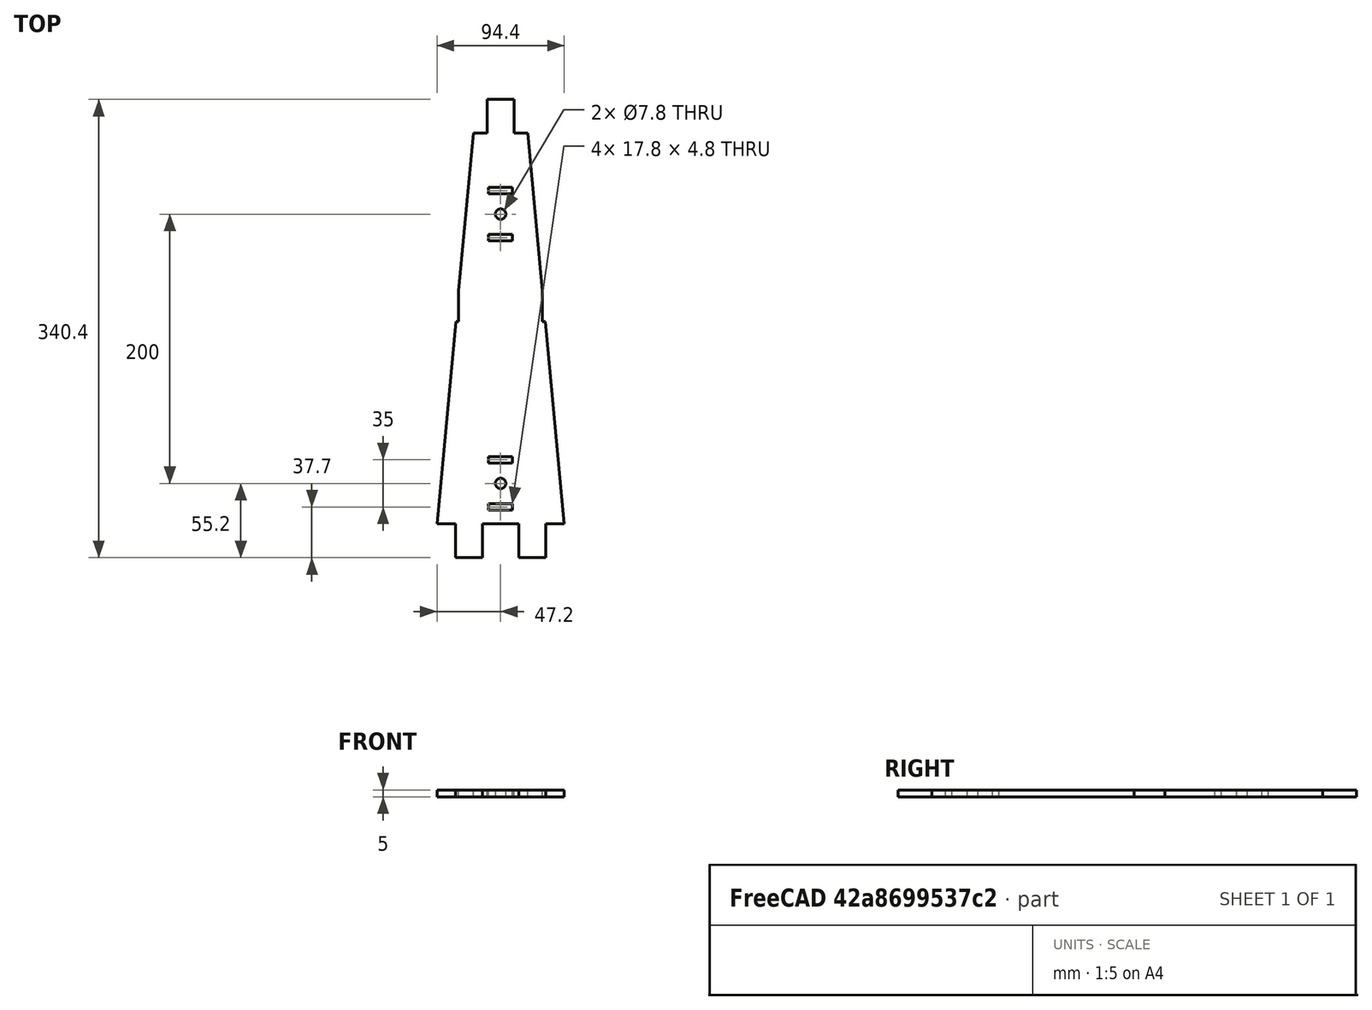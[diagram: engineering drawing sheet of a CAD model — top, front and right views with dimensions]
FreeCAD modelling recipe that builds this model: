
FCSTD DOCUMENT  (FreeCAD 0.16R6712 (Git))
Label: VerticalModded
License: All rights reserved
LicenseURL: http://en.wikipedia.org/wiki/All_rights_reserved
objects: Sketcher::SketchObject×1, PartDesign::Pad×1
note: 3 computed .brp shape members not serialized (recipe doc carries the construction recipe); baked Part::Feature solids carry a one-line shape summary decoded from their .brp

FEATURE [Sketcher::SketchObject] Sketch010
  sketch-geometry (45):
    g0: LineSegment StartX=-10.1 StartY=160.1 StartZ=0 EndX=-20.2 EndY=160.1 EndZ=0
    g1: LineSegment StartX=-20.2 StartY=160.1 StartZ=0 EndX=-31.1 EndY=42.9452 EndZ=0
    g2: LineSegment StartX=-47.2 StartY=-130.1 StartZ=0 EndX=-33.6 EndY=-130.1 EndZ=0
    g3: LineSegment StartX=-33.6 StartY=-130.1 StartZ=0 EndX=-33.6 EndY=-155.2 EndZ=0
    g4: LineSegment StartX=-33.6 StartY=-155.2 StartZ=0 EndX=-13.4 EndY=-155.2 EndZ=0
    g5: LineSegment StartX=-13.4 StartY=-155.2 StartZ=0 EndX=-13.4 EndY=-130.1 EndZ=0
    g6: LineSegment StartX=-13.4 StartY=-130.1 StartZ=0 EndX=13.4 EndY=-130.1 EndZ=0
    g7: LineSegment StartX=13.4 StartY=-130.1 StartZ=0 EndX=13.4 EndY=-155.2 EndZ=0
    g8: LineSegment StartX=13.4 StartY=-155.2 StartZ=0 EndX=33.6 EndY=-155.2 EndZ=0
    g9: LineSegment StartX=33.6 StartY=-155.2 StartZ=0 EndX=33.6 EndY=-130.1 EndZ=0
    g10: LineSegment StartX=33.6 StartY=-130.1 StartZ=0 EndX=47.2 EndY=-130.1 EndZ=0
    g11: LineSegment StartX=47.2 StartY=-130.1 StartZ=0 EndX=33.2255 EndY=20.1 EndZ=0
    g12: LineSegment StartX=20.2 StartY=160.1 StartZ=0 EndX=10.1 EndY=160.1 EndZ=0
    g13: LineSegment StartX=10.1 StartY=160.1 StartZ=0 EndX=10.1 EndY=185.2 EndZ=0
    g14: LineSegment StartX=10.1 StartY=185.2 StartZ=0 EndX=-10.1 EndY=185.2 EndZ=0
    g15: LineSegment StartX=-10.1 StartY=185.2 StartZ=0 EndX=-10.1 EndY=160.1 EndZ=0
    g16: LineSegment [constr] StartX=-140 StartY=-130.1 StartZ=0 EndX=140 EndY=-130.1 EndZ=0
    g17: LineSegment [constr] StartX=-140 StartY=-155.2 StartZ=0 EndX=140 EndY=-155.2 EndZ=0
    g18: LineSegment [constr] StartX=-140 StartY=-100 StartZ=0 EndX=140 EndY=-100 EndZ=0
    g19: Circle CenterX=0 CenterY=-100 CenterZ=0 NormalX=0 NormalY=0 NormalZ=1 Radius=3.9
    g20: LineSegment [constr] StartX=-140 StartY=100 StartZ=0 EndX=140 EndY=100 EndZ=0
    g21: Circle CenterX=0 CenterY=100 CenterZ=0 NormalX=0 NormalY=0 NormalZ=1 Radius=3.9
    g22: LineSegment StartX=-8.9 StartY=119.9 StartZ=0 EndX=8.9 EndY=119.9 EndZ=0
    g23: LineSegment StartX=8.9 StartY=119.9 StartZ=0 EndX=8.9 EndY=115.1 EndZ=0
    g24: LineSegment StartX=8.9 StartY=115.1 StartZ=0 EndX=-8.9 EndY=115.1 EndZ=0
    g25: LineSegment StartX=-8.9 StartY=115.1 StartZ=0 EndX=-8.9 EndY=119.9 EndZ=0
    g26: LineSegment StartX=8.9 StartY=84.9 StartZ=0 EndX=-8.9 EndY=84.9 EndZ=0
    g27: LineSegment StartX=-8.9 StartY=84.9 StartZ=0 EndX=-8.9 EndY=80.1 EndZ=0
    g28: LineSegment StartX=-8.9 StartY=80.1 StartZ=0 EndX=8.9 EndY=80.1 EndZ=0
    g29: LineSegment StartX=8.9 StartY=80.1 StartZ=0 EndX=8.9 EndY=84.9 EndZ=0
    g30: LineSegment StartX=-8.9 StartY=-115.1 StartZ=0 EndX=8.9 EndY=-115.1 EndZ=0
    g31: LineSegment StartX=8.9 StartY=-115.1 StartZ=0 EndX=8.9 EndY=-119.9 EndZ=0
    g32: LineSegment StartX=8.9 StartY=-119.9 StartZ=0 EndX=-8.9 EndY=-119.9 EndZ=0
    g33: LineSegment StartX=-8.9 StartY=-119.9 StartZ=0 EndX=-8.9 EndY=-115.1 EndZ=0
    g34: LineSegment StartX=8.9 StartY=-84.9 StartZ=0 EndX=-8.9 EndY=-84.9 EndZ=0
    g35: LineSegment StartX=-8.9 StartY=-84.9 StartZ=0 EndX=-8.9 EndY=-80.1 EndZ=0
    g36: LineSegment StartX=-8.9 StartY=-80.1 StartZ=0 EndX=8.9 EndY=-80.1 EndZ=0
    g37: LineSegment StartX=8.9 StartY=-80.1 StartZ=0 EndX=8.9 EndY=-84.9 EndZ=0
    g38: LineSegment [constr] StartX=-31.1 StartY=20.1 StartZ=0 EndX=31.1 EndY=20.1 EndZ=0
    g39: LineSegment StartX=-31.1 StartY=20.1 StartZ=0 EndX=-33.2255 EndY=20.1 EndZ=0
    g40: LineSegment StartX=-31.1 StartY=20.1 StartZ=0 EndX=-31.1 EndY=42.9452 EndZ=0
    g41: LineSegment StartX=31.1 StartY=20.1 StartZ=0 EndX=33.2255 EndY=20.1 EndZ=0
    g42: LineSegment StartX=31.1 StartY=20.1 StartZ=0 EndX=31.1 EndY=42.9452 EndZ=0
    g43: LineSegment StartX=-33.2255 StartY=20.1 StartZ=0 EndX=-47.2 EndY=-130.1 EndZ=0
    g44: LineSegment StartX=31.1 StartY=42.9452 StartZ=0 EndX=20.2 EndY=160.1 EndZ=0
  constraints (129):
    c: Horizontal(g0)
    c: Coincident(g0,g1)
    c: Coincident(g43,g2)
    c: Coincident(g2,g3)
    c: Vertical(g3)
    c: Coincident(g3,g4)
    c: Horizontal(g4)
    c: Coincident(g4,g5)
    c: Vertical(g5)
    c: Coincident(g5,g6)
    c: Horizontal(g6)
    c: Coincident(g6,g7)
    c: Vertical(g7)
    c: Coincident(g7,g8)
    c: Horizontal(g8)
    c: Coincident(g8,g9)
    c: Vertical(g9)
    c: Coincident(g9,g10)
    c: Horizontal(g10)
    c: Coincident(g10,g11)
    c: Coincident(g44,g12)
    c: Horizontal(g12)
    c: Coincident(g12,g13)
    c: Vertical(g13)
    c: Coincident(g13,g14)
    c: Horizontal(g14)
    c: Coincident(g14,g15)
    c: Coincident(g15,g0)
    c: Symmetric(g12,g0,g-2)
    c: Vertical(g15)
    c: Symmetric(g44,g0,g-2)
    c: DistanceX(g16) = 140
    c: DistanceY(g16) = -130.1
    c: Symmetric(g16,g16,g-2)
    c: Symmetric(g6,g5,g-2)
    c: Symmetric(g9,g2,g-2)
    c: Symmetric(g10,g43,g-2)
    c: Symmetric(g7,g4,g-2)
    c: Horizontal(g17)
    c: DistanceX(g16,g17) = 0
    c: DistanceY(g17,g16) = 25.1
    c: Symmetric(g17,g17,g-2)
    c: PointOnObject(g4,g17)
    c: DistanceY(g44) = 160.1
    c: DistanceY(g13,g13) = 25.1
    c: DistanceX(g14,g14) = 20.2
    c: DistanceX(g0,g0) = 10.1
    c: PointOnObject(g43,g16)
    c: PointOnObject(g5,g16)
    c: DistanceX(g6,g6) = 26.8
    c: DistanceX(g8,g8) = 20.2
    c: DistanceX(g10,g10) = 13.6
    c: DistanceX(g18,g16) = 0
    c: Symmetric(g18,g18,g-2)
    c: PointOnObject(g19,g18)
    c: PointOnObject(g19,g-2)
    c: Radius(g19) = 3.9
    c: DistanceX(g20,g16) = 0
    c: Symmetric(g20,g20,g-2)
    c: DistanceY(g-1,g20) = 100
    c: PointOnObject(g21,g20)
    c: PointOnObject(g21,g-2)
    c: Radius(g21) = 3.9
    c: Coincident(g22,g23)
    c: Coincident(g23,g24)
    c: Coincident(g24,g25)
    c: Coincident(g25,g22)
    c: Horizontal(g22)
    c: Horizontal(g24)
    c: Vertical(g23)
    c: Vertical(g25)
    c: Coincident(g26,g27)
    c: Coincident(g27,g28)
    c: Coincident(g28,g29)
    c: Coincident(g29,g26)
    c: Horizontal(g26)
    c: Horizontal(g28)
    c: Vertical(g27)
    c: Vertical(g29)
    c: Symmetric(g26,g26,g-2)
    c: Symmetric(g23,g24,g-2)
    c: Symmetric(g26,g23,g20)
    c: Symmetric(g28,g22,g20)
    c: DistanceY(g20,g23) = 15.1
    c: DistanceY(g29,g29) = 4.8
    c: DistanceX(g28,g28) = 17.8
    c: Coincident(g30,g31)
    c: Coincident(g31,g32)
    c: Coincident(g32,g33)
    c: Coincident(g33,g30)
    c: Horizontal(g30)
    c: Horizontal(g32)
    c: Vertical(g31)
    c: Vertical(g33)
    c: Coincident(g34,g35)
    c: Coincident(g35,g36)
    c: Coincident(g36,g37)
    c: Coincident(g37,g34)
    c: Horizontal(g34)
    c: Horizontal(g36)
    c: Vertical(g35)
    c: Vertical(g37)
    c: Symmetric(g34,g34,g-2)
    c: Symmetric(g30,g30,g-2)
    c: Symmetric(g30,g34,g18)
    c: Symmetric(g31,g36,g18)
    c: DistanceY(g18,g34) = 15.1
    c: DistanceY(g31,g31) = 4.8
    c: DistanceX(g36,g36) = 17.8
    c: DistanceX(g4,g4) = 20.2
    c: DistanceY(g19) = -100
    c: Horizontal(g38)
    c: DistanceX(g38,g38) = 62.2
    c: Symmetric(g38,g38,g-2)
    c: DistanceY(g38,g21) = 79.9
    c: Coincident(g39,g38)
    c: Horizontal(g39)
    c: Coincident(g40,g38)
    c: Vertical(g40)
    c: Coincident(g41,g38)
    c: Horizontal(g41)
    c: Coincident(g42,g38)
    c: Vertical(g42)
    c: Coincident(g1,g40)
    c: Coincident(g43,g39)
    c: Tangent(g1,g43)
    c: Coincident(g11,g41)
    c: Coincident(g44,g42)
    c: Tangent(g11,g44)
FEATURE [PartDesign::Pad] Pad010  label="Vertical_A"
  Length = 5
  Length2 = 100
  Sketch = -> Sketch010
  Type = 0
